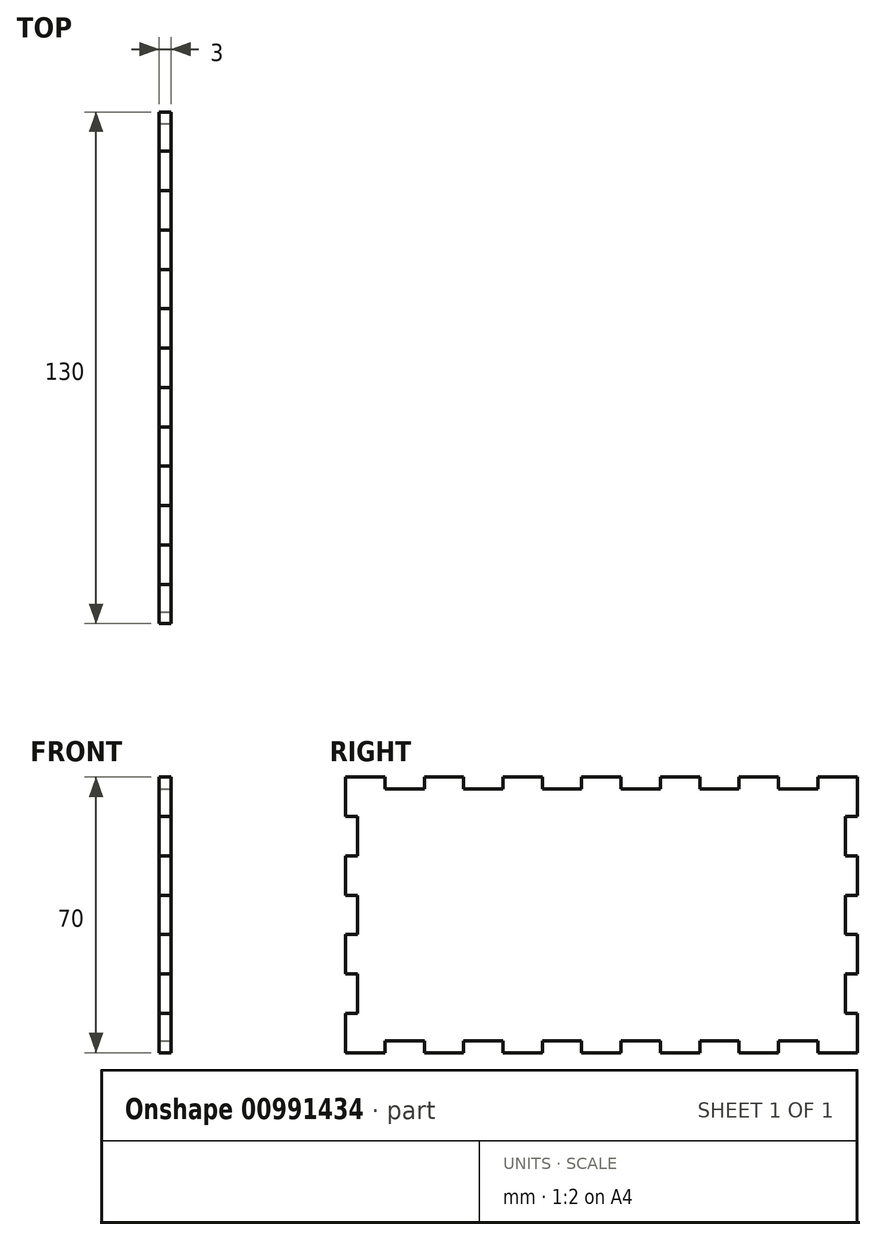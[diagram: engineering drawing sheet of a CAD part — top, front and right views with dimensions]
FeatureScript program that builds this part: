
annotation { "Feature Type Name" : "Feature", "Feature Type Description" : "" }
export const myFeature = defineFeature(function(context is Context, id is Id, definition is map)
    precondition{}
    {
        {
            var Q0;
            Q0=qCreatedBy(makeId("Right.planeOp"),FACE);
            var sketch = newSketch(context, id + "F0", { "sketchPlane" : qUnion([Q0])});
            skLineSegment(sketch, "E0.bottom", {"start": v(65, -35) * mm, "end": v(-65, -35) * mm});
            skLineSegment(sketch, "E0.top", {"start": v(65, 35) * mm, "end": v(-65, 35) * mm});
            skLineSegment(sketch, "E0.left", {"start": v(65, -35) * mm, "end": v(65, 35) * mm});
            skLineSegment(sketch, "E0.right", {"start": v(-65, -35) * mm, "end": v(-65, 35) * mm});
            skPoint(sketch, "E0.middle", {"position": v(0, 0) * mm});
            skSolve(sketch);
        }
        {
            var Q0;
            Q0=qSketchRegion(id+"F0",true);
            extrude(context, id + "F1", {"entities" : qUnion([Q0]), "depth" : 3 * mm, "offsetDistance" : 25 * mm});
        }
        {
            var Q0;
            Q0=makeQuery(id+"F1.opExtrude","CAP_FACE",FACE,{"disambiguationData":[OSD([sQuery(id+"F0.wireOp",EDGE,"E0.bottom"),sQuery(id+"F0.wireOp",EDGE,"E0.top"),sQuery(id+"F0.wireOp",EDGE,"E0.left"),sQuery(id+"F0.wireOp",EDGE,"E0.right")])],"isStart":false});
            var sketch = newSketch(context, id + "F2", { "sketchPlane" : qUnion([Q0])});
            skLineSegment(sketch, "E1.bottom", {"start": v(-65, 25) * mm, "end": v(-62, 25) * mm});
            skLineSegment(sketch, "E1.top", {"start": v(-65, 15) * mm, "end": v(-62, 15) * mm});
            skLineSegment(sketch, "E1.left", {"start": v(-65, 25) * mm, "end": v(-65, 15) * mm});
            skLineSegment(sketch, "E1.right", {"start": v(-62, 25) * mm, "end": v(-62, 15) * mm});
            skLineSegment(sketch, "E2.0.1.0", {"start": v(-65, 5) * mm, "end": v(-65, -5) * mm});
            skLineSegment(sketch, "E2.0.1.1", {"start": v(-65, 5) * mm, "end": v(-62, 5) * mm});
            skLineSegment(sketch, "E2.0.1.2", {"start": v(-62, 5) * mm, "end": v(-62, -5) * mm});
            skLineSegment(sketch, "E2.0.1.3", {"start": v(-65, -5) * mm, "end": v(-62, -5) * mm});
            skLineSegment(sketch, "E2.0.2.0", {"start": v(-65, -15) * mm, "end": v(-65, -25) * mm});
            skLineSegment(sketch, "E2.0.2.1", {"start": v(-65, -15) * mm, "end": v(-62, -15) * mm});
            skLineSegment(sketch, "E2.0.2.2", {"start": v(-62, -15) * mm, "end": v(-62, -25) * mm});
            skLineSegment(sketch, "E2.0.2.3", {"start": v(-65, -25) * mm, "end": v(-62, -25) * mm});
            skLineSegment(sketch, "E2.direction1", {"start": v(-65, 15) * mm, "end": v(-35, 15) * mm, "construction": true});
            skLineSegment(sketch, "E2.direction2", {"start": v(-65, 15) * mm, "end": v(-65, -5) * mm, "construction": true});
            skLineSegment(sketch, "E3", {"start": v(0, 35) * mm, "end": v(0, -35) * mm, "construction": true});
            skLineSegment(sketch, "E4.MirrorCS", {"start": v(65, 5) * mm, "end": v(65, -5) * mm});
            skLineSegment(sketch, "E5.MirrorCS", {"start": v(62, 5) * mm, "end": v(62, -5) * mm});
            skLineSegment(sketch, "E6.MirrorCS", {"start": v(65, -5) * mm, "end": v(62, -5) * mm});
            skLineSegment(sketch, "E7.MirrorCS", {"start": v(65, 15) * mm, "end": v(65, -5) * mm, "construction": true});
            skLineSegment(sketch, "E8.MirrorCS", {"start": v(65, 25) * mm, "end": v(62, 25) * mm});
            skLineSegment(sketch, "E9.MirrorCS", {"start": v(65, -15) * mm, "end": v(65, -25) * mm});
            skLineSegment(sketch, "E10.MirrorCS", {"start": v(65, 15) * mm, "end": v(62, 15) * mm});
            skLineSegment(sketch, "E11.MirrorCS", {"start": v(62, -15) * mm, "end": v(62, -25) * mm});
            skLineSegment(sketch, "E12.MirrorCS", {"start": v(62, 25) * mm, "end": v(62, 15) * mm});
            skLineSegment(sketch, "E13.MirrorCS", {"start": v(65, -25) * mm, "end": v(62, -25) * mm});
            skLineSegment(sketch, "E14.MirrorCS", {"start": v(65, -15) * mm, "end": v(62, -15) * mm});
            skLineSegment(sketch, "E15.MirrorCS", {"start": v(65, 25) * mm, "end": v(65, 15) * mm});
            skLineSegment(sketch, "E16.MirrorCS", {"start": v(65, 5) * mm, "end": v(62, 5) * mm});
            skLineSegment(sketch, "E17", {"start": v(-65, 0) * mm, "end": v(65, 0) * mm, "construction": true});
            skLineSegment(sketch, "E18.bottom", {"start": v(-55, -35) * mm, "end": v(-45, -35) * mm});
            skLineSegment(sketch, "E18.top", {"start": v(-55, -32) * mm, "end": v(-45, -32) * mm});
            skLineSegment(sketch, "E18.left", {"start": v(-55, -35) * mm, "end": v(-55, -32) * mm});
            skLineSegment(sketch, "E18.right", {"start": v(-45, -35) * mm, "end": v(-45, -32) * mm});
            skLineSegment(sketch, "E19.1.0.0", {"start": v(-35, -35) * mm, "end": v(-35, -32) * mm});
            skLineSegment(sketch, "E19.1.0.1", {"start": v(-35, -32) * mm, "end": v(-25, -32) * mm});
            skLineSegment(sketch, "E19.1.0.2", {"start": v(-25, -35) * mm, "end": v(-25, -32) * mm});
            skLineSegment(sketch, "E19.1.0.3", {"start": v(-35, -35) * mm, "end": v(-25, -35) * mm});
            skLineSegment(sketch, "E19.2.0.0", {"start": v(-15, -35) * mm, "end": v(-15, -32) * mm});
            skLineSegment(sketch, "E19.2.0.1", {"start": v(-15, -32) * mm, "end": v(-5, -32) * mm});
            skLineSegment(sketch, "E19.2.0.2", {"start": v(-5, -35) * mm, "end": v(-5, -32) * mm});
            skLineSegment(sketch, "E19.2.0.3", {"start": v(-15, -35) * mm, "end": v(-5, -35) * mm});
            skLineSegment(sketch, "E19.3.0.0", {"start": v(5, -35) * mm, "end": v(5, -32) * mm});
            skLineSegment(sketch, "E19.3.0.1", {"start": v(5, -32) * mm, "end": v(15, -32) * mm});
            skLineSegment(sketch, "E19.3.0.2", {"start": v(15, -35) * mm, "end": v(15, -32) * mm});
            skLineSegment(sketch, "E19.3.0.3", {"start": v(5, -35) * mm, "end": v(15, -35) * mm});
            skLineSegment(sketch, "E19.4.0.0", {"start": v(25, -35) * mm, "end": v(25, -32) * mm});
            skLineSegment(sketch, "E19.4.0.1", {"start": v(25, -32) * mm, "end": v(35, -32) * mm});
            skLineSegment(sketch, "E19.4.0.2", {"start": v(35, -35) * mm, "end": v(35, -32) * mm});
            skLineSegment(sketch, "E19.4.0.3", {"start": v(25, -35) * mm, "end": v(35, -35) * mm});
            skLineSegment(sketch, "E19.5.0.0", {"start": v(45, -35) * mm, "end": v(45, -32) * mm});
            skLineSegment(sketch, "E19.5.0.1", {"start": v(45, -32) * mm, "end": v(55, -32) * mm});
            skLineSegment(sketch, "E19.5.0.2", {"start": v(55, -35) * mm, "end": v(55, -32) * mm});
            skLineSegment(sketch, "E19.5.0.3", {"start": v(45, -35) * mm, "end": v(55, -35) * mm});
            skLineSegment(sketch, "E19.direction1", {"start": v(-55, -35) * mm, "end": v(-35, -35) * mm, "construction": true});
            skLineSegment(sketch, "E20.MirrorCS", {"start": v(-55, 35) * mm, "end": v(-45, 35) * mm});
            skLineSegment(sketch, "E21.MirrorCS", {"start": v(-25, 35) * mm, "end": v(-25, 32) * mm});
            skLineSegment(sketch, "E22.MirrorCS", {"start": v(45, 32) * mm, "end": v(55, 32) * mm});
            skLineSegment(sketch, "E23.MirrorCS", {"start": v(45, 35) * mm, "end": v(55, 35) * mm});
            skLineSegment(sketch, "E24.MirrorCS", {"start": v(-35, 35) * mm, "end": v(-25, 35) * mm});
            skLineSegment(sketch, "E25.MirrorCS", {"start": v(-35, 32) * mm, "end": v(-25, 32) * mm});
            skLineSegment(sketch, "E26.MirrorCS", {"start": v(-5, 35) * mm, "end": v(-5, 32) * mm});
            skLineSegment(sketch, "E27.MirrorCS", {"start": v(-55, 35) * mm, "end": v(-55, 32) * mm});
            skLineSegment(sketch, "E28.MirrorCS", {"start": v(5, 32) * mm, "end": v(15, 32) * mm});
            skLineSegment(sketch, "E29.MirrorCS", {"start": v(55, 35) * mm, "end": v(55, 32) * mm});
            skLineSegment(sketch, "E30.MirrorCS", {"start": v(5, 35) * mm, "end": v(15, 35) * mm});
            skLineSegment(sketch, "E31.MirrorCS", {"start": v(-15, 32) * mm, "end": v(-5, 32) * mm});
            skLineSegment(sketch, "E32.MirrorCS", {"start": v(5, 35) * mm, "end": v(5, 32) * mm});
            skLineSegment(sketch, "E33.MirrorCS", {"start": v(-55, 32) * mm, "end": v(-45, 32) * mm});
            skLineSegment(sketch, "E34.MirrorCS", {"start": v(-55, 35) * mm, "end": v(-35, 35) * mm, "construction": true});
            skLineSegment(sketch, "E35.MirrorCS", {"start": v(35, 35) * mm, "end": v(35, 32) * mm});
            skLineSegment(sketch, "E36.MirrorCS", {"start": v(25, 35) * mm, "end": v(25, 32) * mm});
            skLineSegment(sketch, "E37.MirrorCS", {"start": v(-15, 35) * mm, "end": v(-5, 35) * mm});
            skLineSegment(sketch, "E38.MirrorCS", {"start": v(15, 35) * mm, "end": v(15, 32) * mm});
            skLineSegment(sketch, "E39.MirrorCS", {"start": v(25, 32) * mm, "end": v(35, 32) * mm});
            skLineSegment(sketch, "E40.MirrorCS", {"start": v(-15, 35) * mm, "end": v(-15, 32) * mm});
            skLineSegment(sketch, "E41.MirrorCS", {"start": v(45, 35) * mm, "end": v(45, 32) * mm});
            skLineSegment(sketch, "E42.MirrorCS", {"start": v(-35, 35) * mm, "end": v(-35, 32) * mm});
            skLineSegment(sketch, "E43.MirrorCS", {"start": v(25, 35) * mm, "end": v(35, 35) * mm});
            skLineSegment(sketch, "E44.MirrorCS", {"start": v(-45, 35) * mm, "end": v(-45, 32) * mm});
            skSolve(sketch);
        }
        {
            var Q0;
            Q0=qSketchRegion(id+"F2",true);
            extrude(context, id + "F3", {"entities" : qUnion([Q0]), "operationType" : NewBodyOperationType.REMOVE, "endBound" : BoundingType.THROUGH_ALL, "oppositeDirection" : true, "depth" : 25 * mm, "offsetDistance" : 25 * mm});
        }
    });
